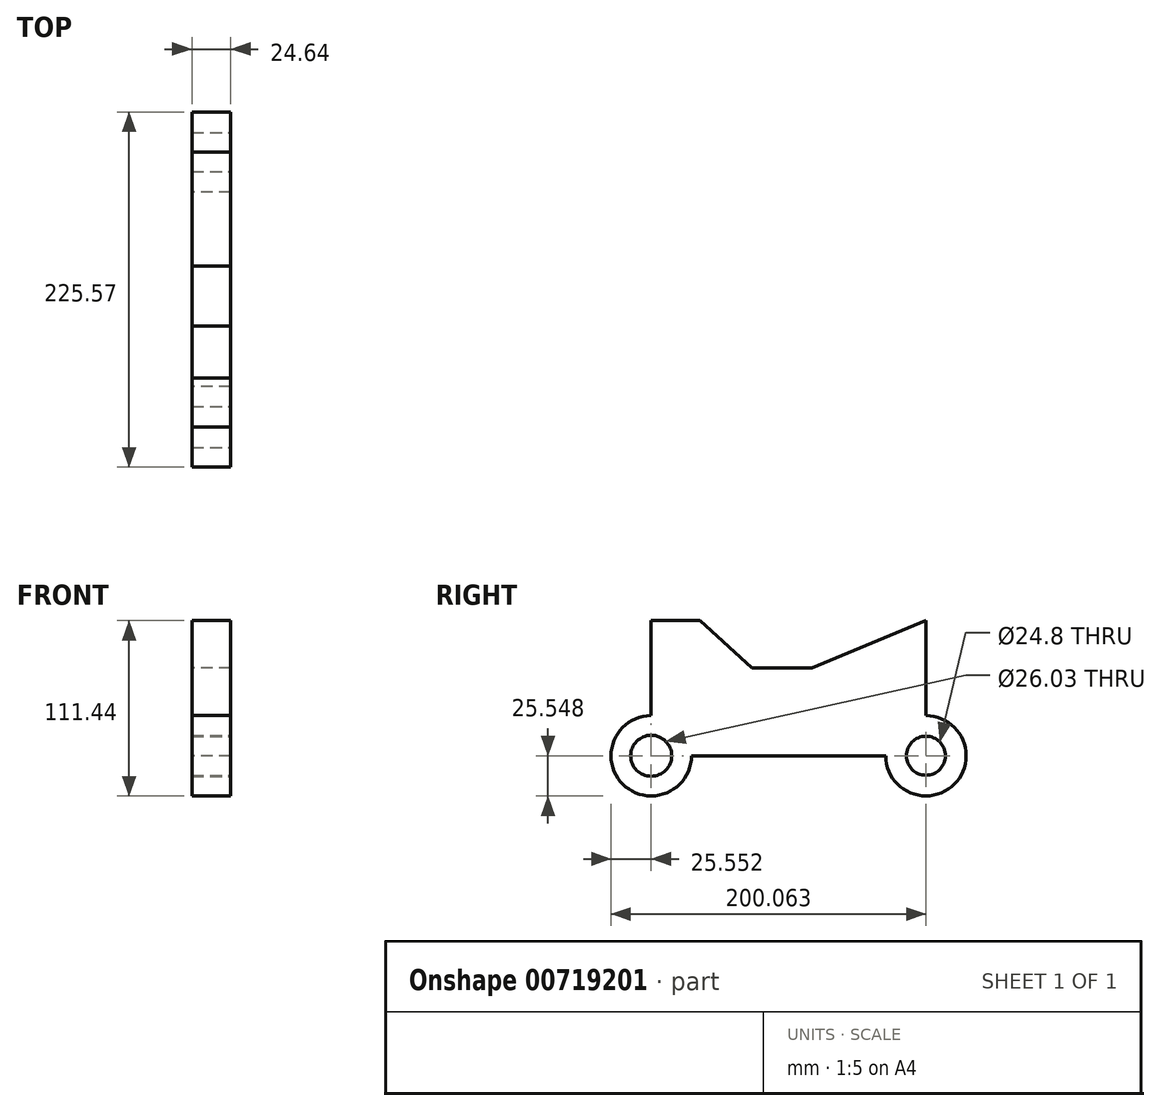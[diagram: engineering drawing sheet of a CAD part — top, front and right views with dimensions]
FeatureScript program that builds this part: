
annotation { "Feature Type Name" : "Feature", "Feature Type Description" : "" }
export const myFeature = defineFeature(function(context is Context, id is Id, definition is map)
    precondition{}
    {
        {
            var Q0;
            Q0=qCreatedBy(makeId("Right.planeOp"),FACE);
            var sketch = newSketch(context, id + "F0", { "sketchPlane" : qUnion([Q0])});
            skLineSegment(sketch, "E0", {"start": v(-109.46, 44.7) * mm, "end": v(-78.28, 44.7) * mm});
            skLineSegment(sketch, "E1", {"start": v(-78.28, 44.7) * mm, "end": v(-45.18, 14.62) * mm});
            skLineSegment(sketch, "E2", {"start": v(-45.18, 14.62) * mm, "end": v(-7.16, 14.62) * mm});
            skLineSegment(sketch, "E3", {"start": v(-7.16, 14.62) * mm, "end": v(65.32, 44.7) * mm});
            skLineSegment(sketch, "E4", {"start": v(65.32, 44.7) * mm, "end": v(65.32, -41.18) * mm});
            skLineSegment(sketch, "E5", {"start": v(65.32, -41.18) * mm, "end": v(-109.19, -41.18) * mm});
            skLineSegment(sketch, "E6", {"start": v(-109.19, -41.18) * mm, "end": v(-109.46, 44.7) * mm});
            skCircle(sketch, "E7", {"center": v(-109.19, -41.18) * mm, "radius": 25.55 * mm});
            skCircle(sketch, "E8", {"center": v(65.32, -41.18) * mm, "radius": 25.5 * mm});
            skSolve(sketch);
        }
        {
            var Q0;
            {var subQ0=sQuery(id+"F0.wireOp",EDGE,"E6");var subQ1=sQuery(id+"F0.wireOp",EDGE,"E5");var subQ2=makeQuery(id+"F0.imprint","INTERSECT",VERTEX,{"derivedFrom":[subQ1,subQ0]});Q0=makeQuery(id+"F0.imprint","IMPRINT",FACE,{"disambiguationData":[TD([[makeQuery(id+"F0.imprint","IMPRINT",EDGE,{"disambiguationData":[TD([[subQ2,1.0]])],"derivedFrom":subQ1}),1.0]])]});}
            var Q1;
            {var subQ0=sQuery(id+"F0.wireOp",EDGE,"E6");var subQ1=sQuery(id+"F0.wireOp",EDGE,"E5");var subQ2=makeQuery(id+"F0.imprint","INTERSECT",VERTEX,{"derivedFrom":[subQ1,subQ0]});Q1=makeQuery(id+"F0.imprint","IMPRINT",FACE,{"disambiguationData":[TD([[makeQuery(id+"F0.imprint","IMPRINT",EDGE,{"disambiguationData":[TD([[subQ2,1.0]])],"derivedFrom":subQ1}),-1.0]])]});}
            var Q2;
            {var subQ6=sQuery(id+"F0.wireOp",EDGE,"E0");Q2=makeQuery(id+"F0.imprint","IMPRINT",FACE,{"disambiguationData":[TD([[makeQuery(id+"F0.imprint","IMPRINT",EDGE,{"derivedFrom":subQ6}),-1.0]])]});}
            var Q3;
            {var subQ0=sQuery(id+"F0.wireOp",EDGE,"E5");var subQ1=sQuery(id+"F0.wireOp",EDGE,"E4");var subQ2=makeQuery(id+"F0.imprint","INTERSECT",VERTEX,{"derivedFrom":[subQ1,subQ0]});Q3=makeQuery(id+"F0.imprint","IMPRINT",FACE,{"disambiguationData":[TD([[makeQuery(id+"F0.imprint","IMPRINT",EDGE,{"disambiguationData":[TD([[subQ2,1.0]])],"derivedFrom":subQ1}),1.0]])]});}
            var Q4;
            {var subQ0=sQuery(id+"F0.wireOp",EDGE,"E5");var subQ1=sQuery(id+"F0.wireOp",EDGE,"E4");var subQ2=makeQuery(id+"F0.imprint","INTERSECT",VERTEX,{"derivedFrom":[subQ1,subQ0]});Q4=makeQuery(id+"F0.imprint","IMPRINT",FACE,{"disambiguationData":[TD([[makeQuery(id+"F0.imprint","IMPRINT",EDGE,{"disambiguationData":[TD([[subQ2,1.0]])],"derivedFrom":subQ1}),-1.0]])]});}
            extrude(context, id + "F1", {"entities" : qUnion([Q0, Q1, Q2, Q3, Q4]), "depth" : 24.64 * mm, "offsetDistance" : 25.4 * mm});
        }
        {
            var Q0;
            Q0=makeQuery(id+"F1.opExtrude","CAP_FACE",FACE,{"disambiguationData":[OSD([sQuery(id+"F0.wireOp",EDGE,"E0"),sQuery(id+"F0.wireOp",EDGE,"E1"),sQuery(id+"F0.wireOp",EDGE,"E2"),sQuery(id+"F0.wireOp",EDGE,"E3"),sQuery(id+"F0.wireOp",EDGE,"E4"),sQuery(id+"F0.wireOp",EDGE,"E5"),sQuery(id+"F0.wireOp",EDGE,"E6"),sQuery(id+"F0.wireOp",EDGE,"E7"),sQuery(id+"F0.wireOp",EDGE,"E8")])],"isStart":false});
            var sketch = newSketch(context, id + "F2", { "sketchPlane" : qUnion([Q0])});
            skCircle(sketch, "E9", {"center": v(-109.19, -41.18) * mm, "radius": 13.02 * mm});
            skCircle(sketch, "E10", {"center": v(65.32, -41.18) * mm, "radius": 12.4 * mm});
            skSolve(sketch);
        }
        {
            var Q0;
            Q0 = qSketchRegion(id + "F2", true);
            extrude(context, id + "F3", {"entities" : qUnion([Q0]), "operationType" : NewBodyOperationType.REMOVE, "oppositeDirection" : true, "depth" : 35.05 * mm, "offsetDistance" : 25.4 * mm});
        }
    });
